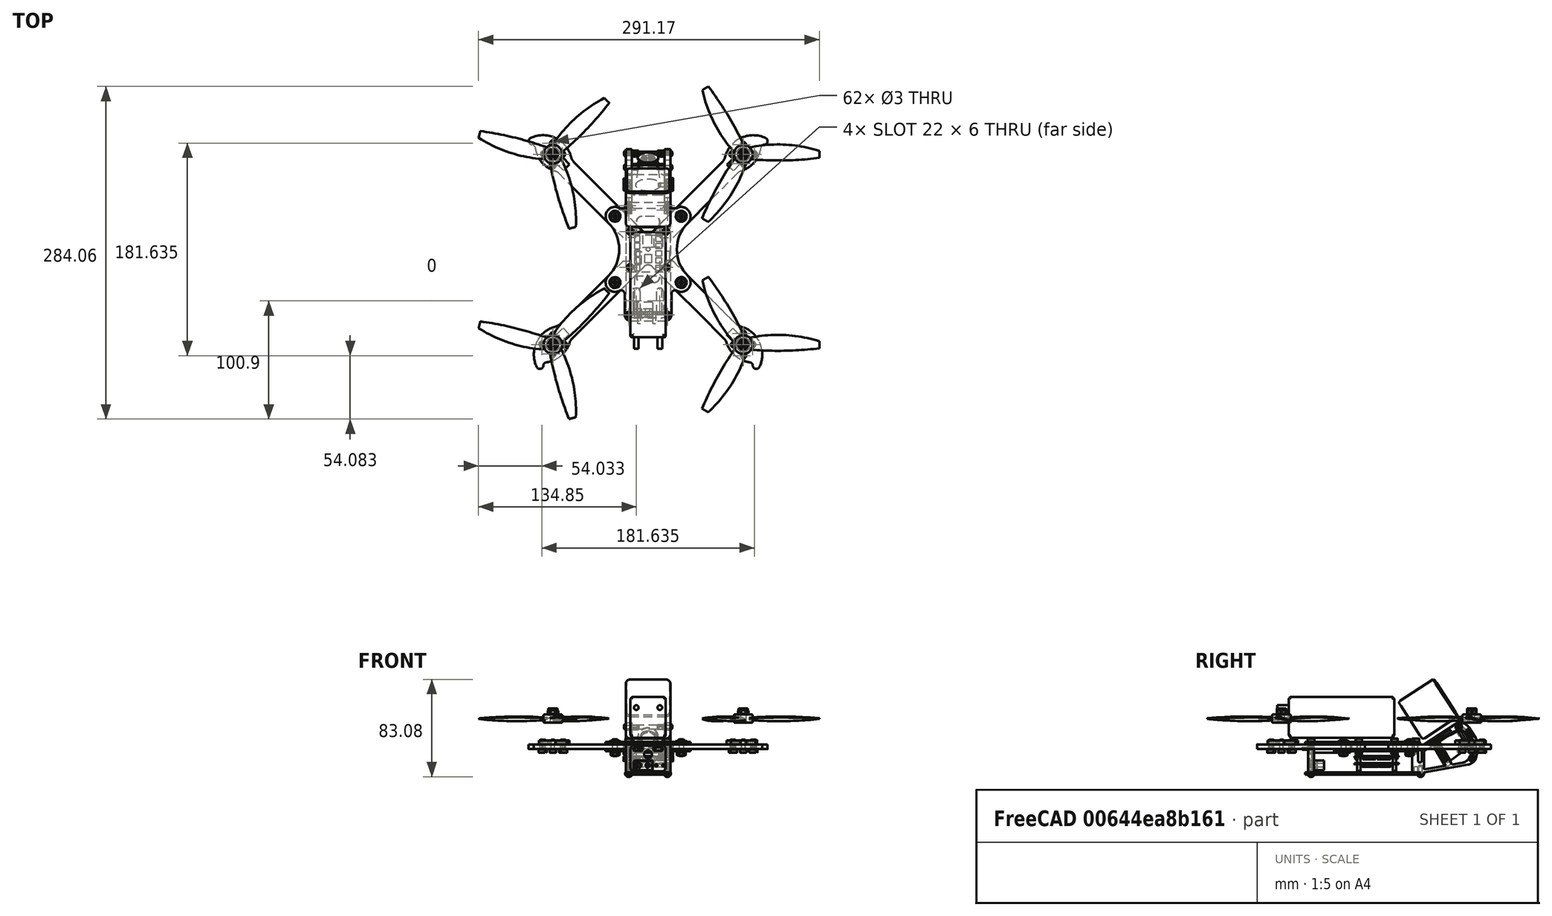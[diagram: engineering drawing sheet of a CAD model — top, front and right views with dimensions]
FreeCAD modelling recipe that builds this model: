
FCSTD DOCUMENT  (FreeCAD 0.18RUnknown)
Label: anomaly
License: All rights reserved
LicenseURL: http://en.wikipedia.org/wiki/All_rights_reserved
objects: Part::FeaturePython×85, App::DocumentObjectGroup×8, Spreadsheet::Sheet×1
note: 85 computed .brp shape members not serialized (recipe doc carries the construction recipe); baked Part::Feature solids carry a one-line shape summary decoded from their .brp

FEATURE [Part::FeaturePython] arm_left_001  # a2plus imported part (geometry in sourceFile) (typed FeaturePython)
  Placement = pos=(-81.3173,81.3173,-4) rot=(0,0,1;0.785398rad)
  a2p_Version = V0.1
  fixedPosition = true
  sourceFile = ./arm_left.fcstd
  subassemblyImport = false
  timeLastImport = 1.56603e+09
  updateColors = true
  expr: Placement.Base.y = Spreadsheet.armOffset
  expr: Placement.Base.x = -Spreadsheet.armOffset
FEATURE [Spreadsheet::Sheet] Spreadsheet
  cells = A1=mLeft; B1=-55; A2=armHoleDist; B2(armHoleDist)=10; D2=armOffsetElectro; E2(armOffsetElectro)==sin(45) * electroMounting; A3=armHoleCenterOffset; B3(armHoleCenterOffset)=40; A4=armLength; B4(armLength)=115; B5(armOffset)==sin(45) * armLength; B6==cos(45) * armLength; A7=motorZ; B7(motorZ)=7; A8==motorMountZ; B8(motorMountZ)=2; A12=bodyWidth; B12(bodyWidth)=38; D12=mountFrontOffset; A13=electroMounting; B13(electroMounting)=30.5; D13=mountBackOffset; A14=electroFCSize; B14(electroFCSize)=38; A15=aluWidth; B15(aluWidth)=5; D15=aluWidthCage; E15(aluWidthCage)=4; A16=aluHeight; B16(aluHeight)=24; A17=aluHoleDist; B17(aluHoleDist)=33; A19=m3taper; B19(m3taper)=1.3
FEATURE [Part::FeaturePython] center_001  # a2plus imported part (geometry in sourceFile) (typed FeaturePython)
  a2p_Version = V0.1
  fixedPosition = false
  sourceFile = ./center.fcstd
  subassemblyImport = false
  timeLastImport = 1.56603e+09
  updateColors = true
FEATURE [Part::FeaturePython] arm_001  # a2plus imported part (geometry in sourceFile) (typed FeaturePython)
  Placement = pos=(81.3173,81.3173,0) rot=(0,0,-1;0.785398rad)
  a2p_Version = V0.1
  fixedPosition = false
  sourceFile = ./arm.fcstd
  subassemblyImport = false
  timeLastImport = 1.56845e+09
  updateColors = true
  expr: Placement.Base.y = Spreadsheet.armOffset
FEATURE [Part::FeaturePython] r6_bottom_001  # a2plus imported part (geometry in sourceFile) (typed FeaturePython)
  Placement = pos=(81.3173,81.3173,0) rot=(0,0,1;3.92699rad)
  a2p_Version = V0.1
  fixedPosition = false
  sourceFile = ./r6_bottom.fcstd
  subassemblyImport = false
  timeLastImport = 1.56603e+09
  updateColors = true
  expr: Placement.Base.y = Spreadsheet.armOffset
FEATURE [Part::FeaturePython] r6_bottom_002  # a2plus imported part (geometry in sourceFile) (typed FeaturePython)
  Placement = pos=(-81.3173,81.3173,0) rot=(0,0,-1;0.785398rad)
  a2p_Version = V0.1
  fixedPosition = false
  sourceFile = ./r6_bottom.fcstd
  subassemblyImport = false
  timeLastImport = 1.56603e+09
  updateColors = true
  expr: Placement.Base.y = Spreadsheet.armOffset
  expr: Placement.Base.x = -Spreadsheet.armOffset
FEATURE [Part::FeaturePython] bottom_001  # a2plus imported part (geometry in sourceFile) (typed FeaturePython)
  Placement = pos=(0,0,-6) rot=(0,0,1;0rad)
  a2p_Version = V0.1
  fixedPosition = false
  sourceFile = ./bottom.fcstd
  subassemblyImport = false
  timeLastImport = 1.56725e+09
  updateColors = true
FEATURE [Part::FeaturePython] cage_001  # a2plus imported part (geometry in sourceFile) (typed FeaturePython)
  Placement = pos=(16.5,35.5,-12) rot=(0,0,1;3.14159rad)
  a2p_Version = V0.1
  fixedPosition = false
  sourceFile = ./cage.fcstd
  subassemblyImport = false
  timeLastImport = 1.56725e+09
  updateColors = true
FEATURE [Part::FeaturePython] cage_002  # a2plus imported part (geometry in sourceFile) (typed FeaturePython)
  Placement = pos=(-16.5,35.5,-12) rot=(0,0,1;3.14159rad)
  a2p_Version = V0.1
  fixedPosition = false
  sourceFile = ./cage.fcstd
  subassemblyImport = false
  timeLastImport = 1.56725e+09
  updateColors = true
FEATURE [Part::FeaturePython] tail_001  # a2plus imported part (geometry in sourceFile) (typed FeaturePython)
  Placement = pos=(0,-56,-12) rot=(0,0,1;0rad)
  a2p_Version = V0.1
  fixedPosition = false
  sourceFile = ./tail.fcstd
  subassemblyImport = false
  timeLastImport = 1.56725e+09
  updateColors = true
FEATURE [Part::FeaturePython] landing_001  # a2plus imported part (geometry in sourceFile) (typed FeaturePython)
  Placement = pos=(0,0,-26) rot=(0,0,1;0rad)
  a2p_Version = V0.1
  fixedPosition = false
  sourceFile = ./landing.fcstd
  subassemblyImport = false
  timeLastImport = 1.56725e+09
  updateColors = true
FEATURE [Part::FeaturePython] foxeer_001  # a2plus imported part (geometry in sourceFile) (typed FeaturePython)
  Placement = pos=(0,55.1,-6.74) rot=(1,0,0;3.66519rad)
  a2p_Version = V0.1
  fixedPosition = false
  sourceFile = ./foxeer.fcstd
  subassemblyImport = false
  timeLastImport = 1.57986e+09
  updateColors = true
FEATURE [Part::FeaturePython] arm_left_002  # a2plus imported part (geometry in sourceFile) (typed FeaturePython)
  Placement = pos=(-81.3173,-81.3173,-4) rot=(0,0,1;2.35619rad)
  a2p_Version = V0.1
  fixedPosition = false
  sourceFile = ./arm_left.fcstd
  subassemblyImport = false
  timeLastImport = 1.56603e+09
  updateColors = true
  expr: Placement.Base.x = -Spreadsheet.armOffset
  expr: Placement.Base.y = -Spreadsheet.armOffset
FEATURE [Part::FeaturePython] r6_bottom_003  # a2plus imported part (geometry in sourceFile) (typed FeaturePython)
  Placement = pos=(-81.3173,-81.3173,0) rot=(0,0,1;0.785398rad)
  a2p_Version = V0.1
  fixedPosition = false
  sourceFile = ./r6_bottom.fcstd
  subassemblyImport = false
  timeLastImport = 1.56603e+09
  updateColors = true
  expr: Placement.Base.x = -Spreadsheet.armOffset
  expr: Placement.Base.y = -Spreadsheet.armOffset
FEATURE [Part::FeaturePython] arm_002  # a2plus imported part (geometry in sourceFile) (typed FeaturePython)
  Placement = pos=(81.3173,-81.3173,0) rot=(0,0,1;3.92699rad)
  a2p_Version = V0.1
  fixedPosition = false
  sourceFile = ./arm.fcstd
  subassemblyImport = false
  timeLastImport = 1.56845e+09
  updateColors = true
  expr: Placement.Base.y = -Spreadsheet.armOffset
  expr: Placement.Base.x = Spreadsheet.armOffset
FEATURE [Part::FeaturePython] r6_bottom_004  # a2plus imported part (geometry in sourceFile) (typed FeaturePython)
  Placement = pos=(81.3173,-81.3173,0) rot=(0,0,1;2.35619rad)
  a2p_Version = V0.1
  fixedPosition = false
  sourceFile = ./r6_bottom.fcstd
  subassemblyImport = false
  timeLastImport = 1.56603e+09
  updateColors = true
  expr: Placement.Base.y = -Spreadsheet.armOffset
  expr: Placement.Base.x = Spreadsheet.armOffset
FEATURE [Part::FeaturePython] r6_001  # a2plus imported part (geometry in sourceFile) (typed FeaturePython)
  Placement = pos=(-81.3173,81.3173,0) rot=(0,0,1;0rad)
  a2p_Version = V0.1
  fixedPosition = false
  sourceFile = ./r6.fcstd
  subassemblyImport = false
  timeLastImport = 1.56603e+09
  updateColors = true
  expr: Placement.Base.y = Spreadsheet.armOffset
  expr: Placement.Base.x = -Spreadsheet.armOffset
FEATURE [Part::FeaturePython] r6_002  # a2plus imported part (geometry in sourceFile) (typed FeaturePython)
  Placement = pos=(-81.3173,-81.3173,0) rot=(0,0,1;0rad)
  a2p_Version = V0.1
  fixedPosition = false
  sourceFile = ./r6.fcstd
  subassemblyImport = false
  timeLastImport = 1.56603e+09
  updateColors = true
  expr: Placement.Base.y = -Spreadsheet.armOffset
  expr: Placement.Base.x = -Spreadsheet.armOffset
FEATURE [Part::FeaturePython] r6_003  # a2plus imported part (geometry in sourceFile) (typed FeaturePython)
  Placement = pos=(81.3173,-81.3173,0) rot=(0,0,1;0rad)
  a2p_Version = V0.1
  fixedPosition = false
  sourceFile = ./r6.fcstd
  subassemblyImport = false
  timeLastImport = 1.56603e+09
  updateColors = true
  expr: Placement.Base.y = -Spreadsheet.armOffset
  expr: Placement.Base.x = Spreadsheet.armOffset
FEATURE [Part::FeaturePython] r6_004  # a2plus imported part (geometry in sourceFile) (typed FeaturePython)
  Placement = pos=(81.3173,81.3173,0) rot=(0,0,1;0rad)
  a2p_Version = V0.1
  fixedPosition = false
  sourceFile = ./r6.fcstd
  subassemblyImport = false
  timeLastImport = 1.56603e+09
  updateColors = true
  expr: Placement.Base.y = Spreadsheet.armOffset
  expr: Placement.Base.x = Spreadsheet.armOffset
FEATURE [Part::FeaturePython] b_xt60_001_  label="xt60_001"  # a2plus imported part (geometry in sourceFile) (typed FeaturePython)
  Placement = pos=(-4,-45,-18) rot=(1,0,0;1.5708rad)
  a2p_Version = V0.1
  fixedPosition = false
  sourceFile = ./xt60.fcstd
  subassemblyImport = false
  timeLastImport = 1.56725e+09
  updateColors = true
FEATURE [Part::FeaturePython] b_d4r2_001_  label="d4r2_001"  # a2plus imported part (geometry in sourceFile) (typed FeaturePython)
  Placement = pos=(0,-38,-3.5) rot=(0,0,1;1.5708rad)
  a2p_Version = V0.1
  fixedPosition = false
  sourceFile = ./d4r2.fcstd
  subassemblyImport = false
  timeLastImport = 1.56725e+09
  updateColors = true
FEATURE [Part::FeaturePython] b_prop_001_  label="prop_001"  # a2plus imported part (geometry in sourceFile) (typed FeaturePython)
  Placement = pos=(-81.3173,-81.3173,22) rot=(0,0,1;0.785398rad)
  a2p_Version = V0.1
  fixedPosition = false
  sourceFile = ./prop.fcstd
  subassemblyImport = false
  timeLastImport = 1.56733e+09
  updateColors = true
  expr: Placement.Base.y = -Spreadsheet.armOffset
  expr: Placement.Base.x = -Spreadsheet.armOffset
FEATURE [App::DocumentObjectGroup] Group006  label="arm_back_left"
  Group = -> [arm_left_002,r6_bottom_003,r6_002,b_prop_001_]
FEATURE [Part::FeaturePython] b_prop_001_001  label="prop_002"  # a2plus imported part (geometry in sourceFile) (typed FeaturePython)
  Placement = pos=(81.3173,-81.3173,22) rot=(0,0,1;0rad)
  a2p_Version = V0.1
  fixedPosition = false
  sourceFile = ./prop.fcstd
  subassemblyImport = false
  timeLastImport = 1.56733e+09
  updateColors = true
  expr: Placement.Base.x = Spreadsheet.armOffset
FEATURE [App::DocumentObjectGroup] Group007  label="arm_back_right"
  Group = -> [arm_002,r6_bottom_004,r6_003,b_prop_001_001]
FEATURE [Part::FeaturePython] b_prop_001_002  label="prop_003"  # a2plus imported part (geometry in sourceFile) (typed FeaturePython)
  Placement = pos=(-81.3173,81.3173,22) rot=(0,0,1;0.785398rad)
  a2p_Version = V0.1
  fixedPosition = false
  sourceFile = ./prop.fcstd
  subassemblyImport = false
  timeLastImport = 1.56733e+09
  updateColors = true
  expr: Placement.Base.y = Spreadsheet.armOffset
  expr: Placement.Base.x = -Spreadsheet.armOffset
FEATURE [App::DocumentObjectGroup] Group003  label="arm_front_left"
  Group = -> [r6_bottom_002,arm_left_001,r6_001,b_prop_001_002]
FEATURE [Part::FeaturePython] b_prop_001_003  label="prop_004"  # a2plus imported part (geometry in sourceFile) (typed FeaturePython)
  Placement = pos=(81.3173,81.3173,22) rot=(0,0,1;0rad)
  a2p_Version = V0.1
  fixedPosition = false
  sourceFile = ./prop.FCStd
  subassemblyImport = false
  timeLastImport = 1.56733e+09
  updateColors = true
  expr: Placement.Base.y = Spreadsheet.armOffset
  expr: Placement.Base.x = Spreadsheet.armOffset
FEATURE [App::DocumentObjectGroup] Group004  label="arm_front_right"
  Group = -> [r6_bottom_001,arm_001,r6_004,b_prop_001_003]
FEATURE [App::DocumentObjectGroup] Group001  label="arms"
  Group = -> [Group003,Group004,Group006,Group007]
FEATURE [App::DocumentObjectGroup] Group005  label="frame"
  Group = -> [center_001,bottom_001,cage_001,cage_002,tail_001,landing_001,Group001]
FEATURE [App::DocumentObjectGroup] Group  label="quad"
  Group = -> [Group005,foxeer_001]
FEATURE [Part::FeaturePython] Screw  label="M4x12-Screw006"  # Fasteners workbench fastener (typed FeaturePython)
  Placement = pos=(-28.2843,28.2843,2) rot=(0,0,1;0rad)
  baseObject = -> center_001 [Edge84]
  diameter = 2
  invert = false
  length = 3
  matchOuter = false
  offset = 0
  thread = false
  type = 21
FEATURE [Part::FeaturePython] Screw001  label="M4x12-Screw005"  # Fasteners workbench fastener (typed FeaturePython)
  Placement = pos=(-28.2843,-28.2843,2) rot=(0,0,1;0rad)
  baseObject = -> center_001 [Edge85]
  diameter = 2
  invert = false
  length = 3
  matchOuter = false
  offset = 0
  thread = false
  type = 21
FEATURE [Part::FeaturePython] Screw002  label="M4x12-Screw"  # Fasteners workbench fastener (typed FeaturePython)
  Placement = pos=(28.2843,-28.2843,2) rot=(0,0,1;0rad)
  baseObject = -> center_001 [Edge92]
  diameter = 2
  invert = false
  length = 3
  matchOuter = false
  offset = 0
  thread = false
  type = 21
FEATURE [Part::FeaturePython] Screw003  label="M4x12-Screw004"  # Fasteners workbench fastener (typed FeaturePython)
  Placement = pos=(28.2843,28.2843,2) rot=(0,0,1;0rad)
  baseObject = -> center_001 [Edge73]
  diameter = 2
  invert = false
  length = 3
  matchOuter = false
  offset = 0
  thread = false
  type = 21
FEATURE [Part::FeaturePython] Screw004  label="M3x25-Screw"  # Fasteners workbench fastener (typed FeaturePython)
  Placement = pos=(-15.25,15.25,2) rot=(0,0,1;0rad)
  baseObject = -> center_001 [Edge83]
  diameter = 4
  invert = false
  length = 8
  matchOuter = false
  offset = 0
  thread = false
  type = 15
FEATURE [Part::FeaturePython] Screw005  label="M3x25-Screw009"  # Fasteners workbench fastener (typed FeaturePython)
  Placement = pos=(15.25,-15.25,2) rot=(0,0,1;0rad)
  baseObject = -> center_001 [Edge82]
  diameter = 4
  invert = false
  length = 8
  matchOuter = false
  offset = 0
  thread = false
  type = 15
FEATURE [Part::FeaturePython] Screw006  label="M3x25-Screw008"  # Fasteners workbench fastener (typed FeaturePython)
  Placement = pos=(15.25,15.25,2) rot=(0,0,1;0rad)
  baseObject = -> center_001 [Edge74]
  diameter = 4
  invert = false
  length = 8
  matchOuter = false
  offset = 0
  thread = false
  type = 15
FEATURE [Part::FeaturePython] Screw007  label="M3x25-Screw007"  # Fasteners workbench fastener (typed FeaturePython)
  Placement = pos=(-15.25,-15.25,2) rot=(0,0,1;0rad)
  baseObject = -> center_001 [Edge81]
  diameter = 4
  invert = false
  length = 8
  matchOuter = false
  offset = 0
  thread = false
  type = 15
FEATURE [Part::FeaturePython] Screw008  label="M3x10-Screw014"  # Fasteners workbench fastener (typed FeaturePython)
  Placement = pos=(-16.5,-56,2) rot=(0,0,1;0rad)
  baseObject = -> center_001 [Edge104]
  diameter = 4
  invert = false
  length = 3
  matchOuter = false
  offset = 0
  thread = false
  type = 15
FEATURE [Part::FeaturePython] Screw009  label="M3x10-Screw013"  # Fasteners workbench fastener (typed FeaturePython)
  Placement = pos=(-16.5,33.5,2) rot=(0,0,1;0rad)
  baseObject = -> center_001 [Edge94]
  diameter = 4
  invert = false
  length = 3
  matchOuter = false
  offset = 0
  thread = false
  type = 15
FEATURE [Part::FeaturePython] Screw010  label="M3x10-Screw"  # Fasteners workbench fastener (typed FeaturePython)
  Placement = pos=(16.5,33.5,2) rot=(0,0,1;0rad)
  baseObject = -> center_001 [Edge93]
  diameter = 4
  invert = false
  length = 3
  matchOuter = false
  offset = 0
  thread = false
  type = 15
FEATURE [Part::FeaturePython] Screw011  label="M3x10-Screw012"  # Fasteners workbench fastener (typed FeaturePython)
  Placement = pos=(16.5,-56,2) rot=(0,0,1;0rad)
  baseObject = -> center_001 [Edge103]
  diameter = 4
  invert = false
  length = 3
  matchOuter = false
  offset = 0
  thread = false
  type = 15
FEATURE [Part::FeaturePython] Screw012  label="M3x8-Screw016"  # Fasteners workbench fastener (typed FeaturePython)
  Placement = pos=(-81.3173,-73.3173,-4) rot=(1,0,0;3.14159rad)
  baseObject = -> arm_left_002 [Edge42]
  diameter = 4
  invert = false
  length = 2
  matchOuter = false
  offset = 0
  thread = false
  type = 15
FEATURE [Part::FeaturePython] Screw013  label="M3x8-Screw018"  # Fasteners workbench fastener (typed FeaturePython)
  Placement = pos=(-90.8173,-81.3173,-4) rot=(1,0,0;3.14159rad)
  baseObject = -> arm_left_002 [Edge45]
  diameter = 4
  invert = false
  length = 2
  matchOuter = false
  offset = 0
  thread = false
  type = 15
FEATURE [Part::FeaturePython] Screw014  label="M3x8-Screw017"  # Fasteners workbench fastener (typed FeaturePython)
  Placement = pos=(-81.3173,-89.3173,-4) rot=(1,0,0;3.14159rad)
  baseObject = -> arm_left_002 [Edge39]
  diameter = 4
  invert = false
  length = 2
  matchOuter = false
  offset = 0
  thread = false
  type = 15
FEATURE [Part::FeaturePython] Screw015  label="M3x8-Screw015"  # Fasteners workbench fastener (typed FeaturePython)
  Placement = pos=(-71.8173,-81.3173,-4) rot=(1,0,0;3.14159rad)
  baseObject = -> arm_left_002 [Edge48]
  diameter = 4
  invert = false
  length = 2
  matchOuter = false
  offset = 0
  thread = false
  type = 15
FEATURE [Part::FeaturePython] Screw016  label="M3x8-Screw019"  # Fasteners workbench fastener (typed FeaturePython)
  Placement = pos=(-73.3173,81.3173,-4) rot=(1,0,0;3.14159rad)
  baseObject = -> arm_left_001 [Edge42]
  diameter = 4
  invert = false
  length = 2
  matchOuter = false
  offset = 0
  thread = false
  type = 15
FEATURE [Part::FeaturePython] Screw017  label="M3x8-Screw014"  # Fasteners workbench fastener (typed FeaturePython)
  Placement = pos=(-81.3173,71.8173,-4) rot=(1,0,0;3.14159rad)
  baseObject = -> arm_left_001 [Edge48]
  diameter = 4
  invert = false
  length = 2
  matchOuter = false
  offset = 0
  thread = false
  type = 15
FEATURE [Part::FeaturePython] Screw018  label="M3x8-Screw013"  # Fasteners workbench fastener (typed FeaturePython)
  Placement = pos=(-89.3173,81.3173,-4) rot=(1,0,0;3.14159rad)
  baseObject = -> arm_left_001 [Edge39]
  diameter = 4
  invert = false
  length = 2
  matchOuter = false
  offset = 0
  thread = false
  type = 15
FEATURE [Part::FeaturePython] Screw019  label="M3x8-Screw012"  # Fasteners workbench fastener (typed FeaturePython)
  Placement = pos=(-81.3173,90.8173,-4) rot=(1,0,0;3.14159rad)
  baseObject = -> arm_left_001 [Edge45]
  diameter = 4
  invert = false
  length = 2
  matchOuter = false
  offset = 0
  thread = false
  type = 15
FEATURE [Part::FeaturePython] Screw020  label="M3x8-Screw046"  # Fasteners workbench fastener (typed FeaturePython)
  Placement = pos=(71.8173,81.3173,-4) rot=(1,0,0;3.14159rad)
  baseObject = -> arm_001 [Edge44]
  diameter = 4
  invert = true
  length = 2
  matchOuter = false
  offset = 0
  thread = false
  type = 15
FEATURE [Part::FeaturePython] Screw021  label="M3x8-Screw045"  # Fasteners workbench fastener (typed FeaturePython)
  Placement = pos=(81.3173,89.3173,-4) rot=(1,0,0;3.14159rad)
  baseObject = -> arm_001 [Edge38]
  diameter = 4
  invert = true
  length = 2
  matchOuter = false
  offset = 0
  thread = false
  type = 15
FEATURE [Part::FeaturePython] Screw022  label="M3x8-Screw044"  # Fasteners workbench fastener (typed FeaturePython)
  Placement = pos=(90.8173,81.3173,-4) rot=(1,0,0;3.14159rad)
  baseObject = -> arm_001 [Edge47]
  diameter = 4
  invert = true
  length = 2
  matchOuter = false
  offset = 0
  thread = false
  type = 15
FEATURE [Part::FeaturePython] Screw023  label="M3x8-Screw043"  # Fasteners workbench fastener (typed FeaturePython)
  Placement = pos=(81.3173,73.3173,-4) rot=(1,0,0;3.14159rad)
  baseObject = -> arm_001 [Edge41]
  diameter = 4
  invert = true
  length = 2
  matchOuter = false
  offset = 0
  thread = false
  type = 15
FEATURE [Part::FeaturePython] Screw024  label="M3x8-Screw042"  # Fasteners workbench fastener (typed FeaturePython)
  Placement = pos=(81.3173,-71.8173,-4) rot=(1,0,0;3.14159rad)
  baseObject = -> arm_002 [Edge44]
  diameter = 4
  invert = true
  length = 2
  matchOuter = false
  offset = 0
  thread = false
  type = 15
FEATURE [Part::FeaturePython] Screw025  label="M3x8-Screw041"  # Fasteners workbench fastener (typed FeaturePython)
  Placement = pos=(73.3173,-81.3173,-4) rot=(1,0,0;3.14159rad)
  baseObject = -> arm_002 [Edge41]
  diameter = 4
  invert = true
  length = 2
  matchOuter = false
  offset = 0
  thread = false
  type = 15
FEATURE [Part::FeaturePython] Screw026  label="M3x8-Screw040"  # Fasteners workbench fastener (typed FeaturePython)
  Placement = pos=(81.3173,-90.8173,-4) rot=(1,0,0;3.14159rad)
  baseObject = -> arm_002 [Edge47]
  diameter = 4
  invert = true
  length = 2
  matchOuter = false
  offset = 0
  thread = false
  type = 15
FEATURE [Part::FeaturePython] Screw027  label="M3x8-Screw039"  # Fasteners workbench fastener (typed FeaturePython)
  Placement = pos=(89.3173,-81.3173,-4) rot=(1,0,0;3.14159rad)
  baseObject = -> arm_002 [Edge38]
  diameter = 4
  invert = true
  length = 2
  matchOuter = false
  offset = 0
  thread = false
  type = 15
FEATURE [Part::FeaturePython] Screw028  label="M3x8-Screw021"  # Fasteners workbench fastener (typed FeaturePython)
  Placement = pos=(16.5,-56,-26) rot=(1,0,0;3.14159rad)
  baseObject = -> landing_001 [Edge47]
  diameter = 1
  invert = true
  length = 1
  matchOuter = false
  offset = 0
  thread = false
  type = 20
FEATURE [Part::FeaturePython] Screw029  label="M3x8-Screw022"  # Fasteners workbench fastener (typed FeaturePython)
  Placement = pos=(-16.5,-56,-26) rot=(1,0,0;3.14159rad)
  baseObject = -> landing_001 [Edge28]
  diameter = 1
  invert = true
  length = 1
  matchOuter = false
  offset = 0
  thread = false
  type = 20
FEATURE [Part::FeaturePython] Screw030  label="M3x8-Screw020"  # Fasteners workbench fastener (typed FeaturePython)
  Placement = pos=(-16.5,37.5,-26) rot=(1,0,0;3.14159rad)
  baseObject = -> landing_001 [Edge49]
  diameter = 1
  invert = true
  length = 1
  matchOuter = false
  offset = 0
  thread = false
  type = 20
FEATURE [Part::FeaturePython] Screw031  label="M3x8-Screw"  # Fasteners workbench fastener (typed FeaturePython)
  Placement = pos=(16.5,37.5,-26) rot=(1,0,0;3.14159rad)
  baseObject = -> landing_001 [Edge48]
  diameter = 1
  invert = true
  length = 1
  matchOuter = false
  offset = 0
  thread = false
  type = 20
FEATURE [Part::FeaturePython] Nut  label="M4-Nut"  # Fasteners workbench fastener (typed FeaturePython)
  Placement = pos=(-28.2843,28.2843,-9.5706) rot=(0,0,1;0rad)
  baseObject = -> Screw [Edge10]
  diameter = 2
  invert = false
  matchOuter = false
  offset = 0
  thread = false
  type = 2
FEATURE [Part::FeaturePython] Nut002  label="M4-Nut005"  # Fasteners workbench fastener (typed FeaturePython)
  Placement = pos=(-28.2843,-28.2843,-9.5706) rot=(0,0,1;0rad)
  baseObject = -> Screw001 [Edge10]
  diameter = 2
  invert = false
  matchOuter = false
  offset = 0
  thread = false
  type = 2
FEATURE [Part::FeaturePython] Nut003  label="M4-Nut004"  # Fasteners workbench fastener (typed FeaturePython)
  Placement = pos=(28.2843,28.2843,-9.5706) rot=(0,0,1;0rad)
  baseObject = -> Screw003 [Edge10]
  diameter = 2
  invert = false
  matchOuter = false
  offset = 0
  thread = false
  type = 2
FEATURE [Part::FeaturePython] Nut004  label="M4-Nut003"  # Fasteners workbench fastener (typed FeaturePython)
  Placement = pos=(28.2843,-28.2843,-9.5706) rot=(0,0,1;0rad)
  baseObject = -> Screw002 [Edge10]
  diameter = 2
  invert = false
  matchOuter = false
  offset = 0
  thread = false
  type = 2
FEATURE [Part::FeaturePython] Nut006  label="M3-Nut"  # Fasteners workbench fastener (typed FeaturePython)
  Placement = pos=(-15.25,15.25,-8.49328) rot=(0,0,1;0rad)
  baseObject = -> Screw004 [Edge14]
  diameter = 4
  invert = false
  matchOuter = false
  offset = 14.2
  thread = false
  type = 4
FEATURE [Part::FeaturePython] Nut010  label="M3-Nut006"  # Fasteners workbench fastener (typed FeaturePython)
  Placement = pos=(15.25,-15.25,-8.49328) rot=(0,0,1;0rad)
  baseObject = -> Screw005 [Edge14]
  diameter = 4
  invert = false
  matchOuter = false
  offset = 14.2
  thread = false
  type = 4
FEATURE [Part::FeaturePython] Nut012  label="M3-Nut005"  # Fasteners workbench fastener (typed FeaturePython)
  Placement = pos=(15.25,15.25,-8.49328) rot=(0,0,1;0rad)
  baseObject = -> Screw006 [Edge14]
  diameter = 4
  invert = false
  matchOuter = false
  offset = 14.2
  thread = false
  type = 4
FEATURE [Part::FeaturePython] Nut008  label="M3-Nut004"  # Fasteners workbench fastener (typed FeaturePython)
  Placement = pos=(-15.25,-15.25,-8.49328) rot=(0,0,1;0rad)
  baseObject = -> Screw007 [Edge14]
  diameter = 4
  invert = false
  matchOuter = false
  offset = 14.2
  thread = false
  type = 4
FEATURE [Part::FeaturePython] Screw032  label="M2x4-Screw"  # Fasteners workbench fastener (typed FeaturePython)
  Placement = pos=(-19,55.5,-6.79067) rot=(0,-1,0;1.5708rad)
  baseObject = -> cage_002 [Edge93]
  diameter = 2
  invert = false
  length = 1
  matchOuter = false
  offset = 0
  thread = false
  type = 15
FEATURE [Part::FeaturePython] Screw034  label="M2x4-Screw002"  # Fasteners workbench fastener (typed FeaturePython)
  Placement = pos=(-19,52.355,-1.34337) rot=(0,-1,0;1.5708rad)
  baseObject = -> cage_002 [Edge91]
  diameter = 2
  invert = false
  length = 1
  matchOuter = false
  offset = 0
  thread = false
  type = 15
FEATURE [Part::FeaturePython] Screw035  label="M2x4-Screw003"  # Fasteners workbench fastener (typed FeaturePython)
  Placement = pos=(-19,58.645,-12.238) rot=(0,-1,0;1.5708rad)
  baseObject = -> cage_002 [Edge92]
  diameter = 2
  invert = false
  length = 1
  matchOuter = false
  offset = 0
  thread = false
  type = 15
FEATURE [Part::FeaturePython] Screw036  label="M2.5x4-Screw004"  # Fasteners workbench fastener (typed FeaturePython)
  Placement = pos=(19,52.355,-1.34337) rot=(0,1,0;1.5708rad)
  baseObject = -> cage_001 [Edge49]
  diameter = 3
  invert = true
  length = 0
  matchOuter = false
  offset = 0
  thread = false
  type = 15
FEATURE [Part::FeaturePython] Screw037  label="M2.5x4-Screw003"  # Fasteners workbench fastener (typed FeaturePython)
  Placement = pos=(19,55.5,-6.79067) rot=(0,1,0;1.5708rad)
  baseObject = -> cage_001 [Edge51]
  diameter = 3
  invert = true
  length = 0
  matchOuter = false
  offset = 0
  thread = false
  type = 15
FEATURE [Part::FeaturePython] Screw038  label="M2.5x4-Screw"  # Fasteners workbench fastener (typed FeaturePython)
  Placement = pos=(19,58.645,-12.238) rot=(0,1,0;1.5708rad)
  baseObject = -> cage_001 [Edge50]
  diameter = 3
  invert = true
  length = 0
  matchOuter = false
  offset = 0
  thread = false
  type = 15
FEATURE [Part::FeaturePython] Nut013  label="M5-Nut"  # Fasteners workbench fastener (typed FeaturePython)
  Placement = pos=(81.3173,81.3173,25.75) rot=(0,0,1;0rad)
  baseObject = -> r6_004 [Edge18]
  diameter = 3
  invert = false
  matchOuter = false
  offset = -5
  thread = false
  type = 2
FEATURE [Part::FeaturePython] Nut014  label="M5-Nut008"  # Fasteners workbench fastener (typed FeaturePython)
  Placement = pos=(-81.3173,81.3173,25.75) rot=(0,0,1;0rad)
  baseObject = -> r6_001 [Edge18]
  diameter = 3
  invert = false
  matchOuter = false
  offset = -5
  thread = false
  type = 2
FEATURE [Part::FeaturePython] Nut015  label="M5-Nut007"  # Fasteners workbench fastener (typed FeaturePython)
  Placement = pos=(81.3173,-81.3173,25.75) rot=(0,0,1;0rad)
  baseObject = -> r6_003 [Edge18]
  diameter = 3
  invert = false
  matchOuter = false
  offset = -5
  thread = false
  type = 2
FEATURE [Part::FeaturePython] Nut016  label="M5-Nut006"  # Fasteners workbench fastener (typed FeaturePython)
  Placement = pos=(-81.3173,-81.3173,25.75) rot=(0,0,1;0rad)
  baseObject = -> r6_002 [Edge18]
  diameter = 3
  invert = false
  matchOuter = false
  offset = -5
  thread = false
  type = 2
FEATURE [Part::FeaturePython] b_standoff_001_  label="standoff_001"  # a2plus imported part (geometry in sourceFile) (typed FeaturePython)
  Placement = pos=(-11,70.3,14.64) rot=(1,0,0;0.523599rad)
  a2p_Version = V0.1
  fixedPosition = false
  sourceFile = ./standoff.fcstd
  subassemblyImport = false
  timeLastImport = 1.56733e+09
  updateColors = true
FEATURE [Part::FeaturePython] b_standoff_001_001  label="standoff_002"  # a2plus imported part (geometry in sourceFile) (typed FeaturePython)
  Placement = pos=(-11,81.8185,-11.9289) rot=(-1,0,0;0.471239rad)
  a2p_Version = V0.1
  fixedPosition = false
  sourceFile = ./standoff.fcstd
  subassemblyImport = false
  timeLastImport = 1.56733e+09
  updateColors = true
FEATURE [Part::FeaturePython] Screw039  label="M3x10-Screw009"  # Fasteners workbench fastener (typed FeaturePython)
  Placement = pos=(-19,81.8648,-11.958) rot=(0,-1,0;1.5708rad)
  baseObject = -> cage_002 [Edge90]
  diameter = 1
  invert = false
  length = 2
  matchOuter = false
  offset = 0
  thread = false
  type = 20
FEATURE [Part::FeaturePython] Screw040  label="M3x10-Screw008"  # Fasteners workbench fastener (typed FeaturePython)
  Placement = pos=(-19,70.184,14.9829) rot=(0,-1,0;1.5708rad)
  baseObject = -> cage_002 [Edge89]
  diameter = 1
  invert = false
  length = 2
  matchOuter = false
  offset = 0
  thread = false
  type = 20
FEATURE [Part::FeaturePython] Screw041  label="M3x10-Screw011"  # Fasteners workbench fastener (typed FeaturePython)
  Placement = pos=(19,81.8648,-11.958) rot=(0,1,0;1.5708rad)
  baseObject = -> cage_001 [Edge48]
  diameter = 1
  invert = true
  length = 2
  matchOuter = false
  offset = 0
  thread = false
  type = 20
FEATURE [Part::FeaturePython] Screw042  label="M3x10-Screw010"  # Fasteners workbench fastener (typed FeaturePython)
  Placement = pos=(19,70.184,14.9829) rot=(0,1,0;1.5708rad)
  baseObject = -> cage_001 [Edge47]
  diameter = 1
  invert = true
  length = 2
  matchOuter = false
  offset = 0
  thread = false
  type = 20
FEATURE [App::DocumentObjectGroup] Group008  label="fasteners"
  Group = -> [Screw,Screw001,Screw002,Screw003,Screw004,Screw005,Screw006,Screw007,Screw008,Screw009,Screw010,Screw011,Screw012,Screw013,Screw014,Screw015,Screw016,Screw017,Screw018,Screw019,Screw020,Screw021,Screw022,Screw023,Screw024,Screw025,Screw026,Screw027,Screw028,Screw029,Screw030,Screw031,Nut,Nut002,Nut003,Nut004,Nut006,Nut010,Nut012,Nut008,Screw032,Screw034,Screw035,Screw036,Screw037,Screw038,Nut013,+7 more]
FEATURE [Part::FeaturePython] b_fc_001_  label="fc_001"  # a2plus imported part (geometry in sourceFile) (typed FeaturePython)
  Placement = pos=(0,0,-16.11) rot=(1,0,0;3.14159rad)
  a2p_Version = V0.1
  fixedPosition = false
  sourceFile = ./fc.fcstd
  subassemblyImport = false
  timeLastImport = 1.56837e+09
  updateColors = true
FEATURE [Part::FeaturePython] b_esc_001_  label="esc_001"  # a2plus imported part (geometry in sourceFile) (typed FeaturePython)
  Placement = pos=(0,0,-10) rot=(1,0,0;3.14159rad)
  a2p_Version = V0.1
  fixedPosition = false
  sourceFile = ./esc.fcstd
  sourcePart = Body
  subassemblyImport = false
  timeLastImport = 1.56837e+09
  updateColors = true
FEATURE [Part::FeaturePython] b_lipo_001_  label="lipo_001"  # a2plus imported part (geometry in sourceFile) (typed FeaturePython)
  Placement = pos=(0,-30,0) rot=(0,0,1;1.5708rad)
  a2p_Version = V0.1
  fixedPosition = false
  sourceFile = ./lipo.fcstd
  subassemblyImport = false
  timeLastImport = 1.5684e+09
  updateColors = true
FEATURE [Part::FeaturePython] b_gopro_001_  label="gopro_001"  # a2plus imported part (geometry in sourceFile) (typed FeaturePython)
  Placement = pos=(0,59.37,40) rot=(1,0,0;0.575959rad)
  a2p_Version = V0.1
  fixedPosition = false
  sourceFile = ./gopro.fcstd
  subassemblyImport = false
  timeLastImport = 1.57986e+09
  updateColors = true
